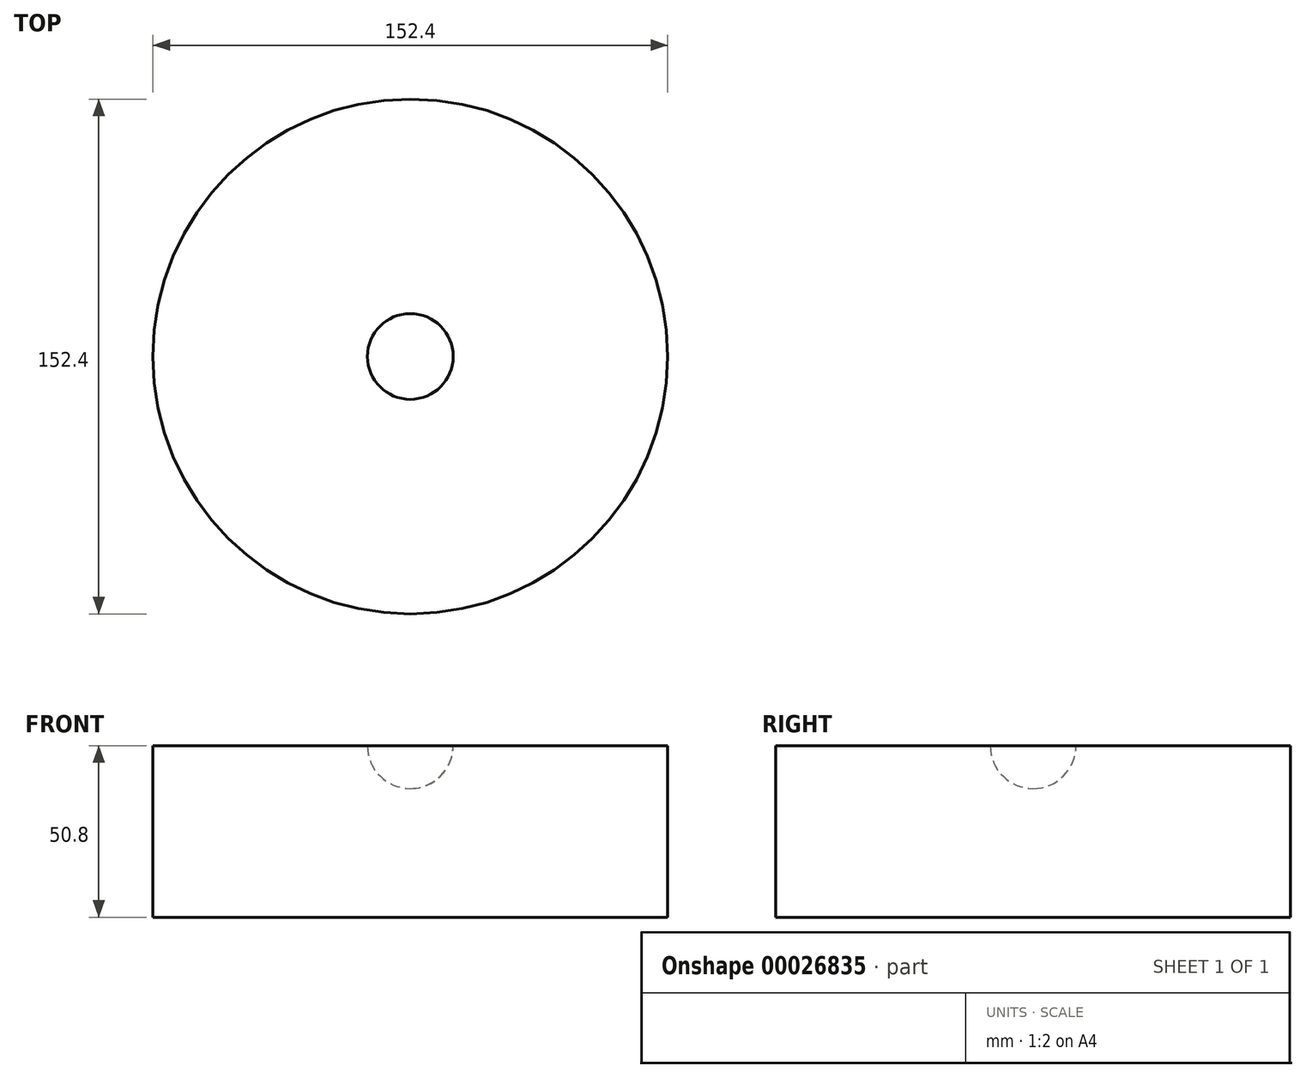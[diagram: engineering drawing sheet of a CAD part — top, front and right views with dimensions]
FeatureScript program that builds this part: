
annotation { "Feature Type Name" : "Feature", "Feature Type Description" : "" }
export const myFeature = defineFeature(function(context is Context, id is Id, definition is map)
    precondition{}
    {
        {
            var Q0;
            Q0=qCreatedBy(makeId("Front.planeOp"),FACE);
            var sketch = newSketch(context, id + "F0", { "sketchPlane" : qUnion([Q0])});
            skArc(sketch, "E0", {"start": v(0, -12.7) * mm, "mid": v(8.98, -8.98) * mm, "end": v(12.7, 0) * mm});
            skPoint(sketch, "E1", {"position": v(12.7, 0) * mm});
            skPoint(sketch, "E2", {"position": v(0, -12.7) * mm});
            skLineSegment(sketch, "E3.bottom", {"start": v(12.7, 0) * mm, "end": v(76.2, 0) * mm});
            skLineSegment(sketch, "E3.top", {"start": v(0, -50.8) * mm, "end": v(76.2, -50.8) * mm});
            skLineSegment(sketch, "E3.left", {"start": v(0, -12.7) * mm, "end": v(0, -50.8) * mm});
            skLineSegment(sketch, "E3.right", {"start": v(76.2, 0) * mm, "end": v(76.2, -50.8) * mm});
            skSolve(sketch);
        }
        {
            var Q0;
            Q0=makeQuery(id+"F0.imprint","IMPRINT",FACE,{"disambiguationData":[TD([[makeQuery(id+"F0.imprint","IMPRINT",EDGE,{"derivedFrom":sQuery(id+"F0.wireOp",EDGE,"E0")}),-1.0]])]});
            var Q1;
            Q1=sQuery(id+"F0.wireOp",EDGE,"E3.left");
            revolve(context, id + "F1", {"entities" : qUnion([Q0]), "axis" : qUnion([Q1]), "revolveType" : RevolveType.FULL});
        }
    });
